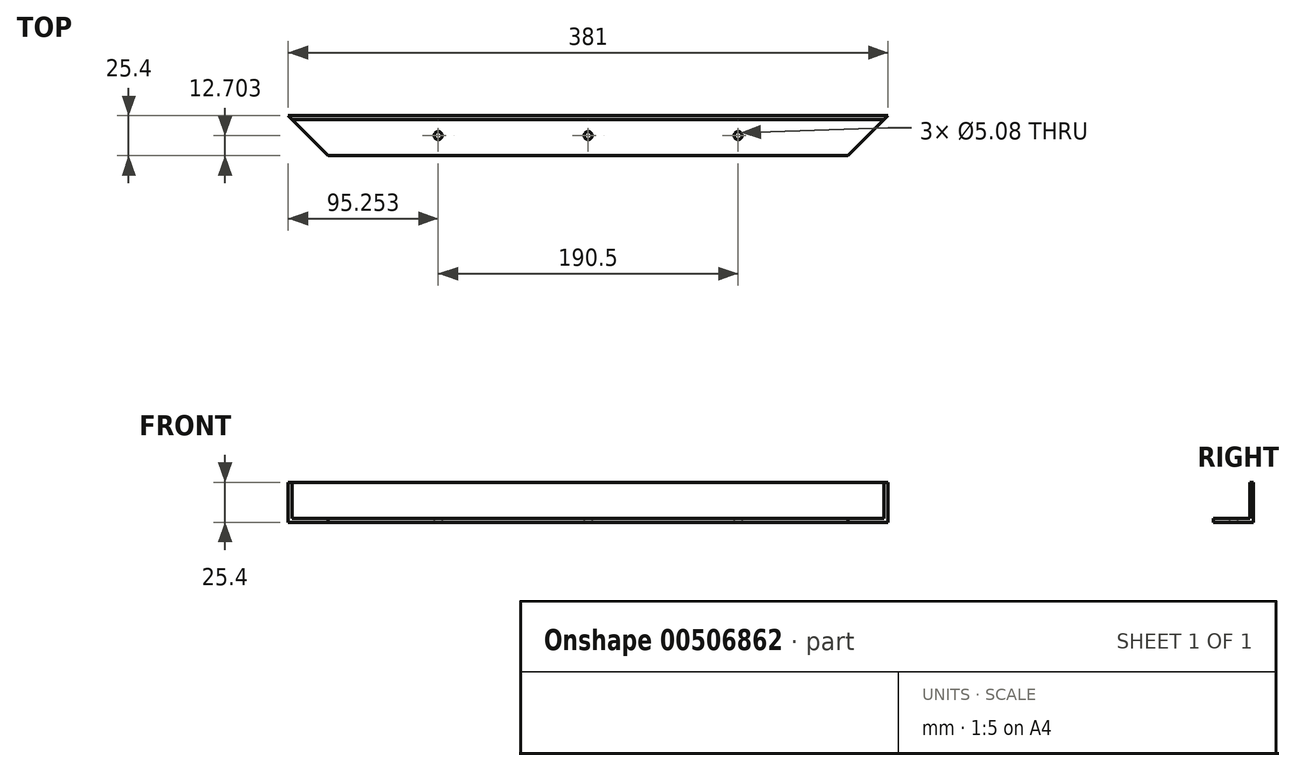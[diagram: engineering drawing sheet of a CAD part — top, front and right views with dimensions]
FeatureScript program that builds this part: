
annotation { "Feature Type Name" : "Feature", "Feature Type Description" : "" }
export const myFeature = defineFeature(function(context is Context, id is Id, definition is map)
    precondition{}
    {
        {
            var Q0;
            Q0=qCreatedBy(makeId("Top.planeOp"),FACE);
            var sketch = newSketch(context, id + "F0", { "sketchPlane" : qUnion([Q0])});
            skLineSegment(sketch, "E0.bottom", {"start": v(-196.82, -10.25) * mm, "end": v(184.18, -10.25) * mm});
            skLineSegment(sketch, "E0.top", {"start": v(-196.82, -35.65) * mm, "end": v(184.18, -35.65) * mm});
            skLineSegment(sketch, "E0.left", {"start": v(-196.82, -10.25) * mm, "end": v(-196.82, -35.65) * mm});
            skLineSegment(sketch, "E0.right", {"start": v(184.18, -10.25) * mm, "end": v(184.18, -35.65) * mm});
            skPoint(sketch, "E1", {"position": v(158.78, -35.65) * mm});
            skPoint(sketch, "E2", {"position": v(-171.42, -35.65) * mm});
            skLineSegment(sketch, "E3", {"start": v(-196.82, -10.25) * mm, "end": v(-171.42, -35.65) * mm});
            skLineSegment(sketch, "E4", {"start": v(184.18, -10.25) * mm, "end": v(158.78, -35.65) * mm});
            skPoint(sketch, "E5", {"position": v(-101.57, -10.25) * mm});
            skPoint(sketch, "E6", {"position": v(-6.32, -10.25) * mm});
            skPoint(sketch, "E7", {"position": v(88.93, -10.25) * mm});
            skLineSegment(sketch, "E8", {"start": v(-101.57, -10.25) * mm, "end": v(-101.57, -35.65) * mm, "construction": true});
            skLineSegment(sketch, "E9", {"start": v(-6.32, -10.25) * mm, "end": v(-6.32, -35.65) * mm, "construction": true});
            skLineSegment(sketch, "E10", {"start": v(88.93, -10.25) * mm, "end": v(88.93, -35.65) * mm, "construction": true});
            skCircle(sketch, "E11", {"center": v(-101.57, -22.95) * mm, "radius": 2.54 * mm});
            skCircle(sketch, "E12", {"center": v(-6.32, -22.95) * mm, "radius": 2.54 * mm});
            skCircle(sketch, "E13", {"center": v(88.93, -22.95) * mm, "radius": 2.54 * mm});
            skSolve(sketch);
        }
        {
            var Q0;
            Q0=makeQuery(id+"F0.imprint","IMPRINT",FACE,{"disambiguationData":[TD([[makeQuery(id+"F0.imprint","IMPRINT",EDGE,{"derivedFrom":sQuery(id+"F0.wireOp",EDGE,"E0.bottom")}),-1.0]])]});
            extrude(context, id + "F1", {"entities" : qUnion([Q0]), "depth" : 25.4 * mm, "offsetDistance" : 25.4 * mm});
        }
        {
            var Q0;
            Q0=makeQuery(id+"F1.opExtrude","SWEPT_FACE",FACE,{"disambiguationData":[OSD([sQuery(id+"F0.wireOp",EDGE,"E11")])]});
            var Q1;
            Q1=makeQuery(id+"F1.opExtrude","SWEPT_FACE",FACE,{"disambiguationData":[OSD([sQuery(id+"F0.wireOp",EDGE,"E12")])]});
            var Q2;
            Q2=makeQuery(id+"F1.opExtrude","SWEPT_FACE",FACE,{"disambiguationData":[OSD([sQuery(id+"F0.wireOp",EDGE,"E13")])]});
            var Q3;
            Q3=makeQuery(id+"F1.opExtrude","SWEPT_FACE",FACE,{"disambiguationData":[OSD([sQuery(id+"F0.wireOp",EDGE,"E3")])]});
            var Q4;
            Q4=makeQuery(id+"F1.opExtrude","SWEPT_FACE",FACE,{"disambiguationData":[OSD([sQuery(id+"F0.wireOp",EDGE,"E4")])]});
            var Q5;
            Q5=makeQuery(id+"F1.opExtrude","SWEPT_FACE",FACE,{"disambiguationData":[OSD([sQuery(id+"F0.wireOp",EDGE,"E0.top")])]});
            var Q6;
            Q6=makeQuery(id+"F1.opExtrude","CAP_FACE",FACE,{"disambiguationData":[OSD([sQuery(id+"F0.wireOp",EDGE,"E0.bottom"),sQuery(id+"F0.wireOp",EDGE,"E0.top"),sQuery(id+"F0.wireOp",EDGE,"E3"),sQuery(id+"F0.wireOp",EDGE,"E4"),sQuery(id+"F0.wireOp",EDGE,"E11"),sQuery(id+"F0.wireOp",EDGE,"E12"),sQuery(id+"F0.wireOp",EDGE,"E13")])],"isStart":false});
            shell(context, id + "F2", {"entities" : qUnion([Q0, Q1, Q2, Q3, Q4, Q5, Q6]), "thickness" : 2.54 * mm});
        }
    });
